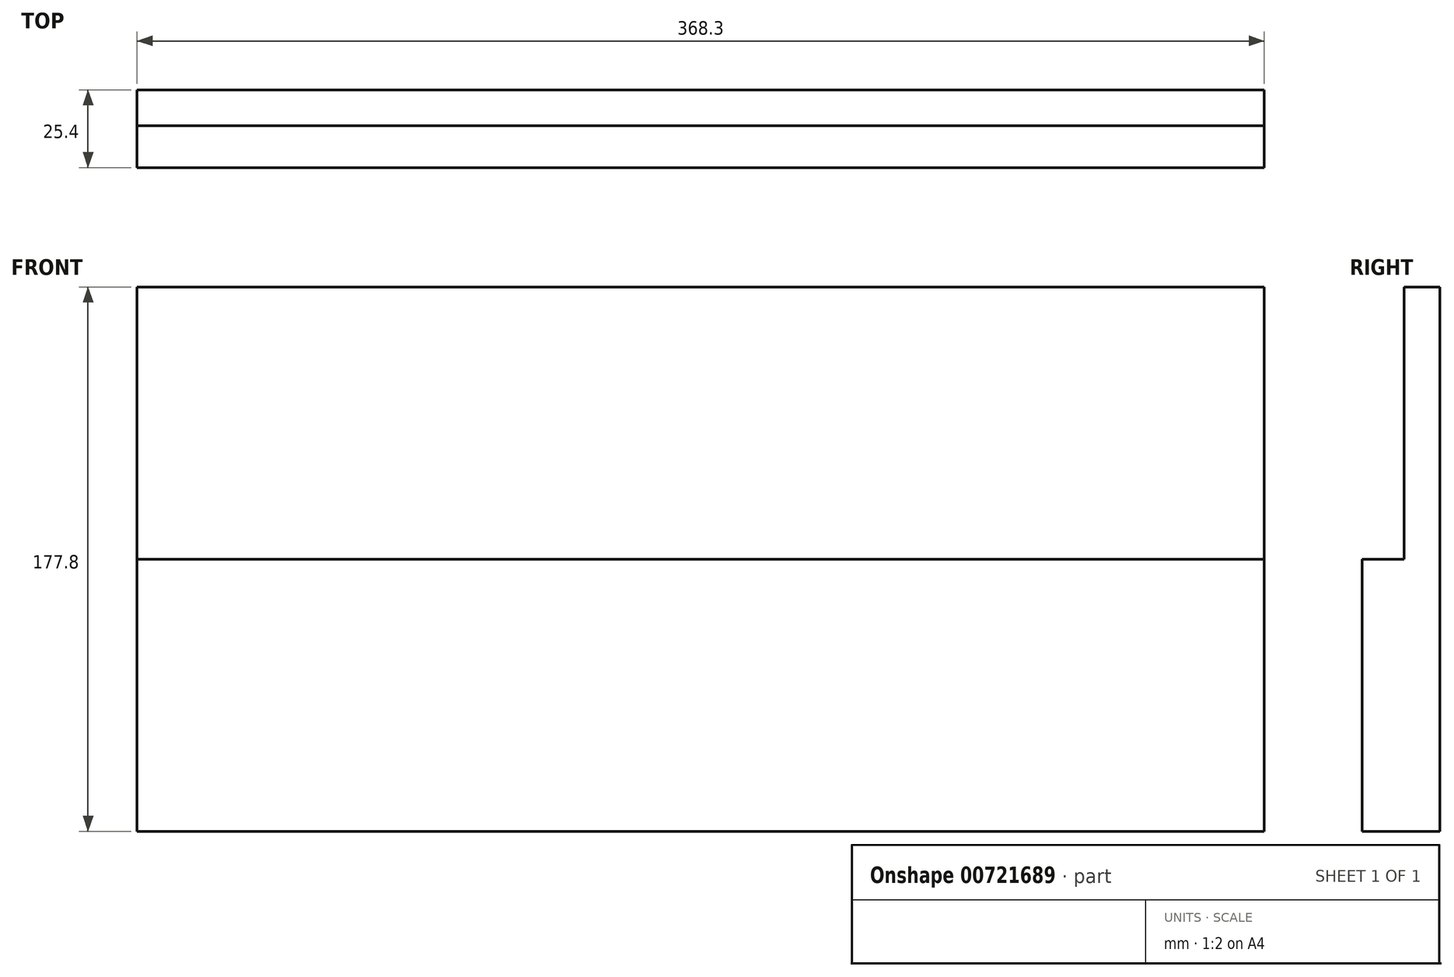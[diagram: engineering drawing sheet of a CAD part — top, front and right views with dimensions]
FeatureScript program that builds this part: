
annotation { "Feature Type Name" : "Feature", "Feature Type Description" : "" }
export const myFeature = defineFeature(function(context is Context, id is Id, definition is map)
    precondition{}
    {
        {
            var Q0;
            Q0=qCreatedBy(makeId("Front.planeOp"),FACE);
            var sketch = newSketch(context, id + "F0", { "sketchPlane" : qUnion([Q0])});
            skLineSegment(sketch, "E0.bottom", {"start": v(0, 0) * mm, "end": v(368.3, 0) * mm});
            skLineSegment(sketch, "E0.top", {"start": v(0, -177.8) * mm, "end": v(368.3, -177.8) * mm});
            skLineSegment(sketch, "E0.left", {"start": v(0, 0) * mm, "end": v(0, -177.8) * mm});
            skLineSegment(sketch, "E0.right", {"start": v(368.3, 0) * mm, "end": v(368.3, -177.8) * mm});
            skSolve(sketch);
        }
        {
            var Q0;
            Q0=makeQuery(id+"F0.imprint","IMPRINT",FACE,{"disambiguationData":[TD([[makeQuery(id+"F0.imprint","IMPRINT",EDGE,{"derivedFrom":sQuery(id+"F0.wireOp",EDGE,"E0.bottom")}),-1.0]])]});
            extrude(context, id + "F1", {"entities" : qUnion([Q0]), "depth" : 25.4 * mm, "offsetDistance" : 25.4 * mm});
        }
        {
            var Q0;
            Q0=qCreatedBy(makeId("Right.planeOp"),FACE);
            var sketch = newSketch(context, id + "F2", { "sketchPlane" : qUnion([Q0])});
            skLineSegment(sketch, "E1.bottom", {"start": v(-11.69, -88.9) * mm, "end": v(-108.76, -88.9) * mm});
            skLineSegment(sketch, "E1.top", {"start": v(-11.69, 0) * mm, "end": v(-108.76, 0) * mm});
            skLineSegment(sketch, "E1.left", {"start": v(-11.69, -88.9) * mm, "end": v(-11.69, 0) * mm});
            skLineSegment(sketch, "E1.right", {"start": v(-108.76, -88.9) * mm, "end": v(-108.76, 0) * mm});
            skPoint(sketch, "E1.middle", {"position": v(-60.23, -44.45) * mm});
            skSolve(sketch);
        }
        {
            var Q0;
            Q0=makeQuery(id+"F2.imprint","IMPRINT",FACE,{"disambiguationData":[TD([[makeQuery(id+"F2.imprint","IMPRINT",EDGE,{"derivedFrom":sQuery(id+"F2.wireOp",EDGE,"E1.bottom")}),-1.0]])]});
            extrude(context, id + "F3", {"entities" : qUnion([Q0]), "operationType" : NewBodyOperationType.REMOVE, "depth" : 368.3 * mm, "offsetDistance" : 25.4 * mm});
        }
    });
